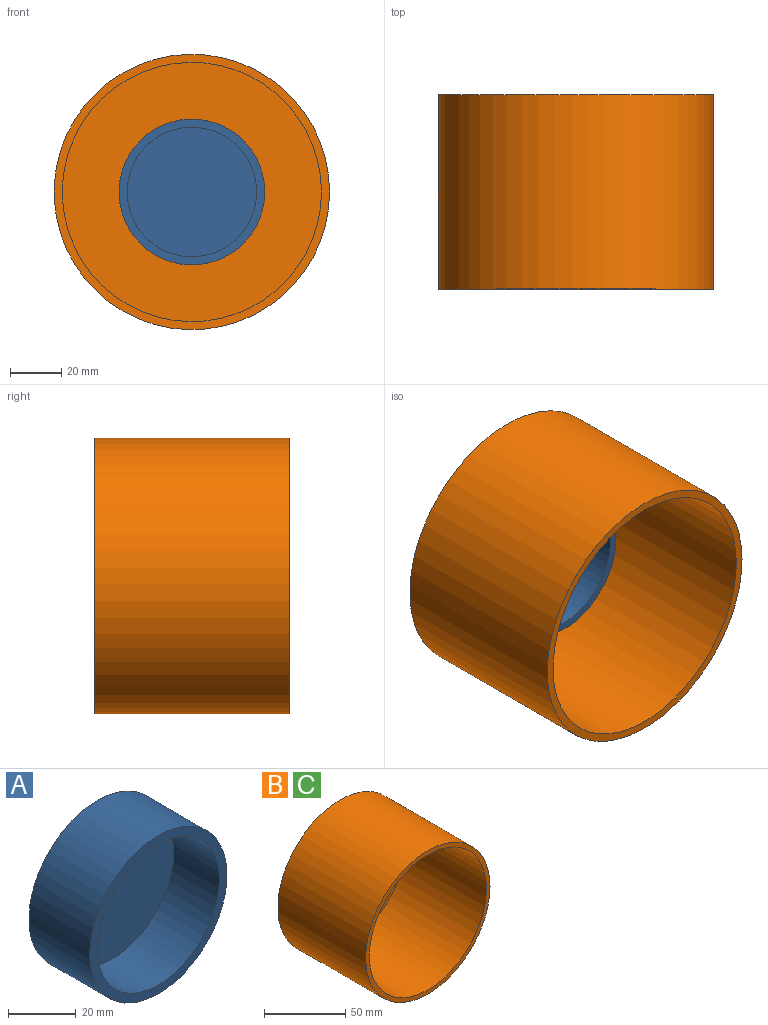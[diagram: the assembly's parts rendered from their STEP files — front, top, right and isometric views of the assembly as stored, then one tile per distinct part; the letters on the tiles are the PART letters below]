
ASSEMBLY  parts=3 mates=1
PART A: 5 faces, bbox 57.2x25.4x57.2 mm
  f0: cylinder r=25.4mm len=50.8mm, axis (0,1,0), area 3040.2mm2, adj f2,f4
  f1: cylinder r=28.57mm len=57.15mm, axis (0,1,0), area 4560.4mm2, adj f2,f3
  f2: plane 57.15x57.15mm, normal (0,-1,0), area 538.4mm2, adj f0,f1
  f3: plane 57.15x57.15mm, normal (0,1,0), area 2565.2mm2, adj f1
  f4: plane 50.8x50.8mm, normal (0,-1,0), area 2026.8mm2, adj f0
PART B: 5 faces, bbox 108x76.2x108 mm
  f0: cylinder r=50.8mm len=101.6mm, axis (0,1,0), area 22295.1mm2, adj f2,f4
  f1: cylinder r=53.98mm len=107.95mm, axis (0,1,0), area 25842.1mm2, adj f2,f3
  f2: plane 107.95x107.95mm, normal (0,-1,0), area 1045.1mm2, adj f0,f1
  f3: plane 107.95x107.95mm, normal (0,1,0), area 9152.4mm2, adj f1
  f4: plane 101.6x101.6mm, normal (0,-1,0), area 8107.3mm2, adj f0
PART C: same geometry as B
PLACE A t=(-83.21,49.47,85.21)mm
PLACE B t=(-83.21,55.82,85.21)mm
PLACE C t=(-83.21,55.82,85.21)mm
MATE slider A.f0 <-> C.f0  axis (0,1,0) through (-83.21,49.47,85.21)mm
